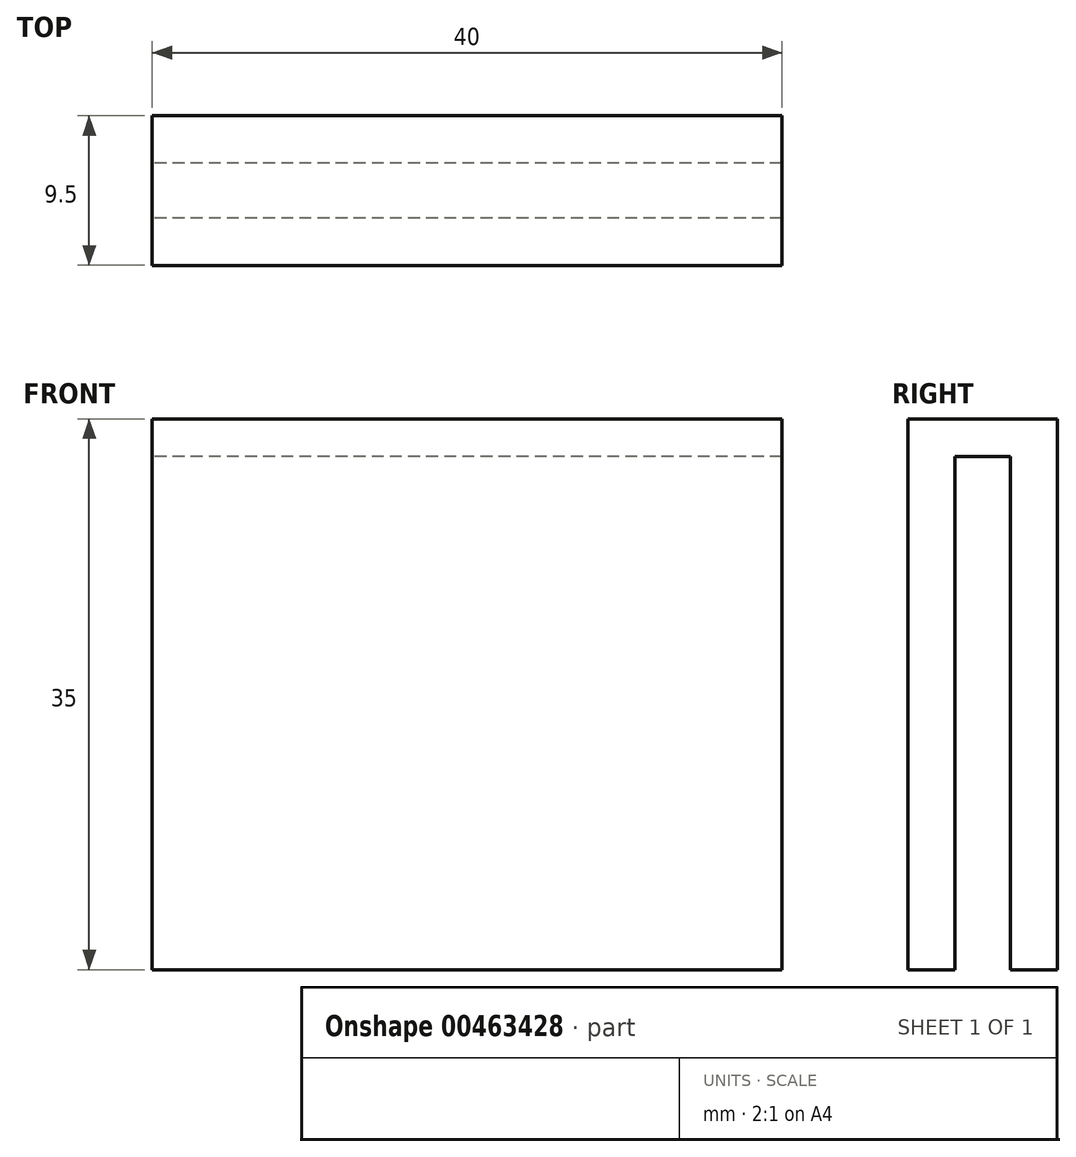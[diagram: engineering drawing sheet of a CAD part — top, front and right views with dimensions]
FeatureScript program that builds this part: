
annotation { "Feature Type Name" : "Feature", "Feature Type Description" : "" }
export const myFeature = defineFeature(function(context is Context, id is Id, definition is map)
    precondition{}
    {
        {
            var Q0;
            Q0=qCreatedBy(makeId("Right.planeOp"),FACE);
            var sketch = newSketch(context, id + "F0", { "sketchPlane" : qUnion([Q0])});
            skLineSegment(sketch, "E0", {"start": v(-3.5, -35) * mm, "end": v(-0.5, -35) * mm});
            skLineSegment(sketch, "E1", {"start": v(-0.5, -35) * mm, "end": v(-0.5, -2.4) * mm});
            skLineSegment(sketch, "E2", {"start": v(-0.5, -2.4) * mm, "end": v(3, -2.4) * mm});
            skLineSegment(sketch, "E3", {"start": v(3, -2.4) * mm, "end": v(3, -35) * mm});
            skLineSegment(sketch, "E4", {"start": v(3, -35) * mm, "end": v(6, -35) * mm});
            skLineSegment(sketch, "E5", {"start": v(6, -35) * mm, "end": v(6, 0) * mm});
            skLineSegment(sketch, "E6", {"start": v(6, 0) * mm, "end": v(-3.5, 0) * mm});
            skLineSegment(sketch, "E7", {"start": v(-3.5, 0) * mm, "end": v(-3.5, -35) * mm});
            skSolve(sketch);
        }
        {
            var Q0;
            Q0 = qSketchRegion(id + "F0", true);
            extrude(context, id + "F1", {"entities" : qUnion([Q0]), "endBound" : BoundingType.SYMMETRIC, "depth" : 40 * mm});
        }
    });
